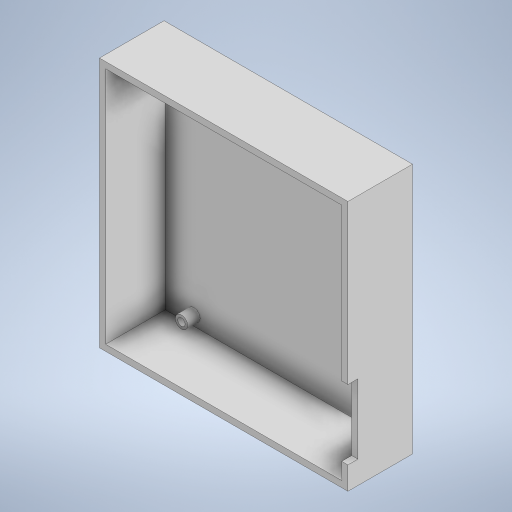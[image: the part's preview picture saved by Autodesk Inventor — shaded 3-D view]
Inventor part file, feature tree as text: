
AUTODESK INVENTOR PART (.ipt)
format: ipt  version: 2023 (Build 270158000, 158)  size: 584,192 bytes
history: native  units: mm
features: extrude x4, sketch x4, other x1
ambient origin geometry x8: Origin, YZ Plane, XZ Plane, XY Plane, X Axis, Y Axis, Z Axis, Center Point
bodies: Body1 (feature_tree)
feature tree (9):
  other  "Sólido1"
  extrude  "Base"  Depth=101.0mm
  extrude  "Área"  Depth=2.5mm
  extrude  "Extrusão3"  Depth=24.0mm
  extrude  "Extrusão4"  Depth=28.0mm
  sketch  "Esboço1"  dims[d0=100.0mm d1=101.0mm]
  sketch  "Esboço2"  dims[d2=26.0mm d3=0.0mm d4=2.5mm]
  sketch  "Esboço3"  dims[d5=24.0mm d6=0.0mm d11=3.0mm]
  sketch  "Esboço4"  dims[d12=14.0mm d13=6.5mm d14=5.0mm d15=5.0mm d16=0.0mm d17=4.0mm d18=28.0mm d19=0.0mm d20=0.0mm]
